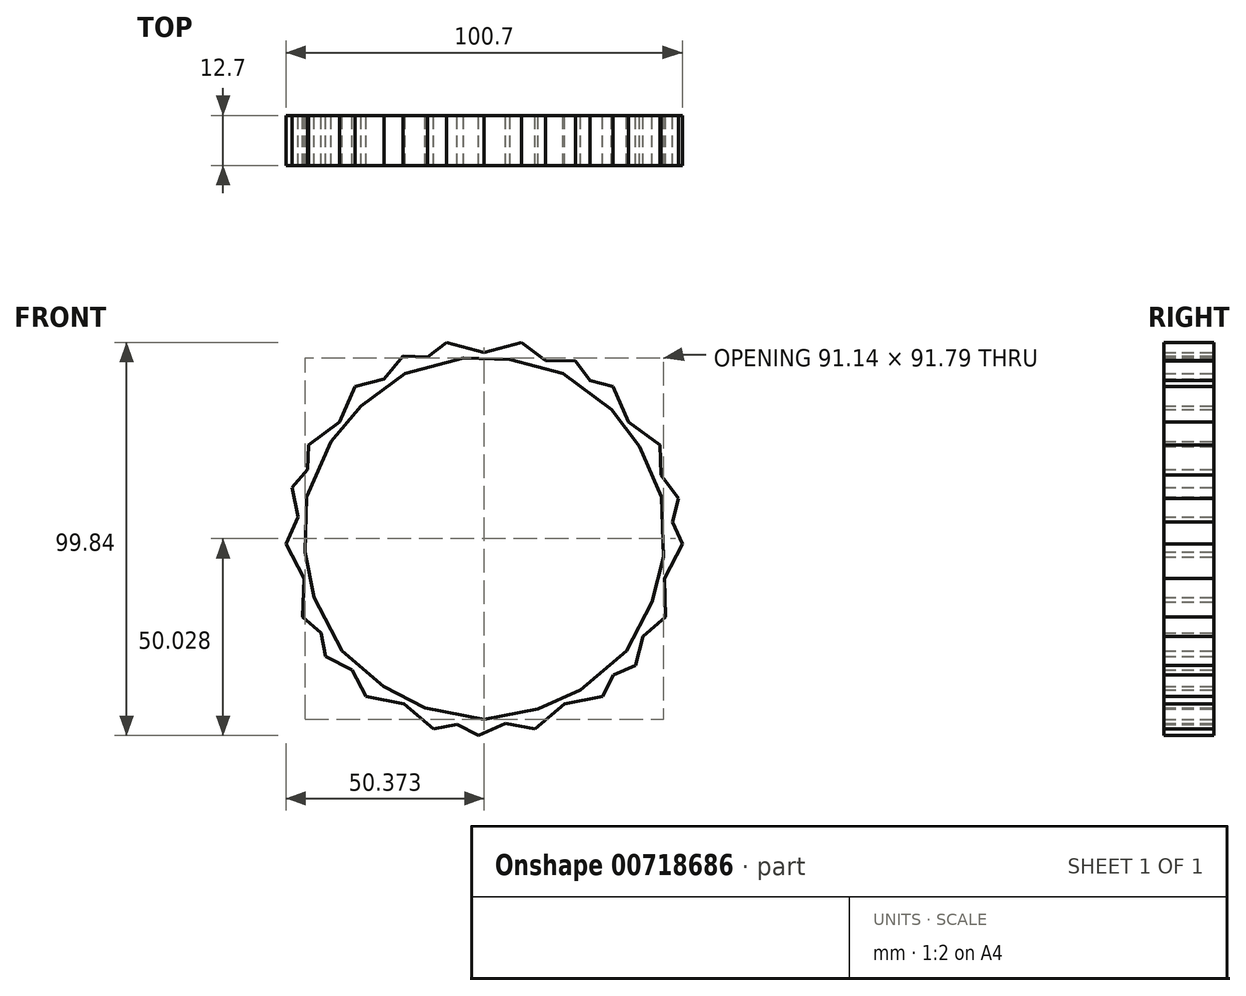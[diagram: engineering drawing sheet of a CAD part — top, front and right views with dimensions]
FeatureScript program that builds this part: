
annotation { "Feature Type Name" : "Feature", "Feature Type Description" : "" }
export const myFeature = defineFeature(function(context is Context, id is Id, definition is map)
    precondition{}
    {
        {
            var Q0;
            Q0=qCreatedBy(makeId("Front.planeOp"),FACE);
            var sketch = newSketch(context, id + "F0", { "sketchPlane" : qUnion([Q0])});
            skCircle(sketch, "E0.cCircle", {"center": v(0, 0) * mm, "radius": 50.38 * mm, "construction": true});
            skLineSegment(sketch, "E0.0", {"start": v(32.75, 38.29) * mm, "end": v(50.35, -1.73) * mm});
            skLineSegment(sketch, "E0.1", {"start": v(50.35, -1.73) * mm, "end": v(30.04, -40.45) * mm});
            skLineSegment(sketch, "E0.2", {"start": v(30.04, -40.45) * mm, "end": v(-12.9, -48.7) * mm});
            skLineSegment(sketch, "E0.3", {"start": v(-12.9, -48.7) * mm, "end": v(-46.12, -20.29) * mm});
            skLineSegment(sketch, "E0.4", {"start": v(-46.12, -20.29) * mm, "end": v(-44.61, 23.4) * mm});
            skLineSegment(sketch, "E0.5", {"start": v(-44.61, 23.4) * mm, "end": v(-9.52, 49.48) * mm});
            skLineSegment(sketch, "E0.6", {"start": v(-9.52, 49.48) * mm, "end": v(32.75, 38.29) * mm});
            skLineSegment(sketch, "E1.0", {"start": v(9.52, 49.48) * mm, "end": v(44.61, 23.4) * mm});
            skLineSegment(sketch, "E1.1", {"start": v(44.61, 23.4) * mm, "end": v(46.12, -20.29) * mm});
            skLineSegment(sketch, "E1.2", {"start": v(46.12, -20.29) * mm, "end": v(12.9, -48.7) * mm});
            skLineSegment(sketch, "E1.3", {"start": v(12.9, -48.7) * mm, "end": v(-30.04, -40.45) * mm});
            skLineSegment(sketch, "E1.4", {"start": v(-30.04, -40.45) * mm, "end": v(-50.35, -1.73) * mm});
            skLineSegment(sketch, "E1.5", {"start": v(-50.35, -1.73) * mm, "end": v(-32.75, 38.29) * mm});
            skLineSegment(sketch, "E1.6", {"start": v(-32.75, 38.29) * mm, "end": v(9.52, 49.48) * mm});
            skLineSegment(sketch, "E2.0", {"start": v(-20.56, 46) * mm, "end": v(23.14, 44.75) * mm});
            skLineSegment(sketch, "E2.1", {"start": v(23.14, 44.75) * mm, "end": v(49.42, 9.8) * mm});
            skLineSegment(sketch, "E2.2", {"start": v(49.42, 9.8) * mm, "end": v(38.48, -32.52) * mm});
            skLineSegment(sketch, "E2.3", {"start": v(38.48, -32.52) * mm, "end": v(-1.43, -50.36) * mm});
            skLineSegment(sketch, "E2.4", {"start": v(-1.43, -50.36) * mm, "end": v(-40.27, -30.28) * mm});
            skLineSegment(sketch, "E2.5", {"start": v(-40.27, -30.28) * mm, "end": v(-48.78, 12.6) * mm});
            skLineSegment(sketch, "E2.6", {"start": v(-48.78, 12.6) * mm, "end": v(-20.56, 46) * mm});
            skSolve(sketch);
        }
        {
            var Q0;
            Q0 = qSketchRegion(id + "F0", true);
            extrude(context, id + "F1", {"entities" : qUnion([Q0]), "depth" : 12.7 * mm, "offsetDistance" : 25.4 * mm});
        }
    });
